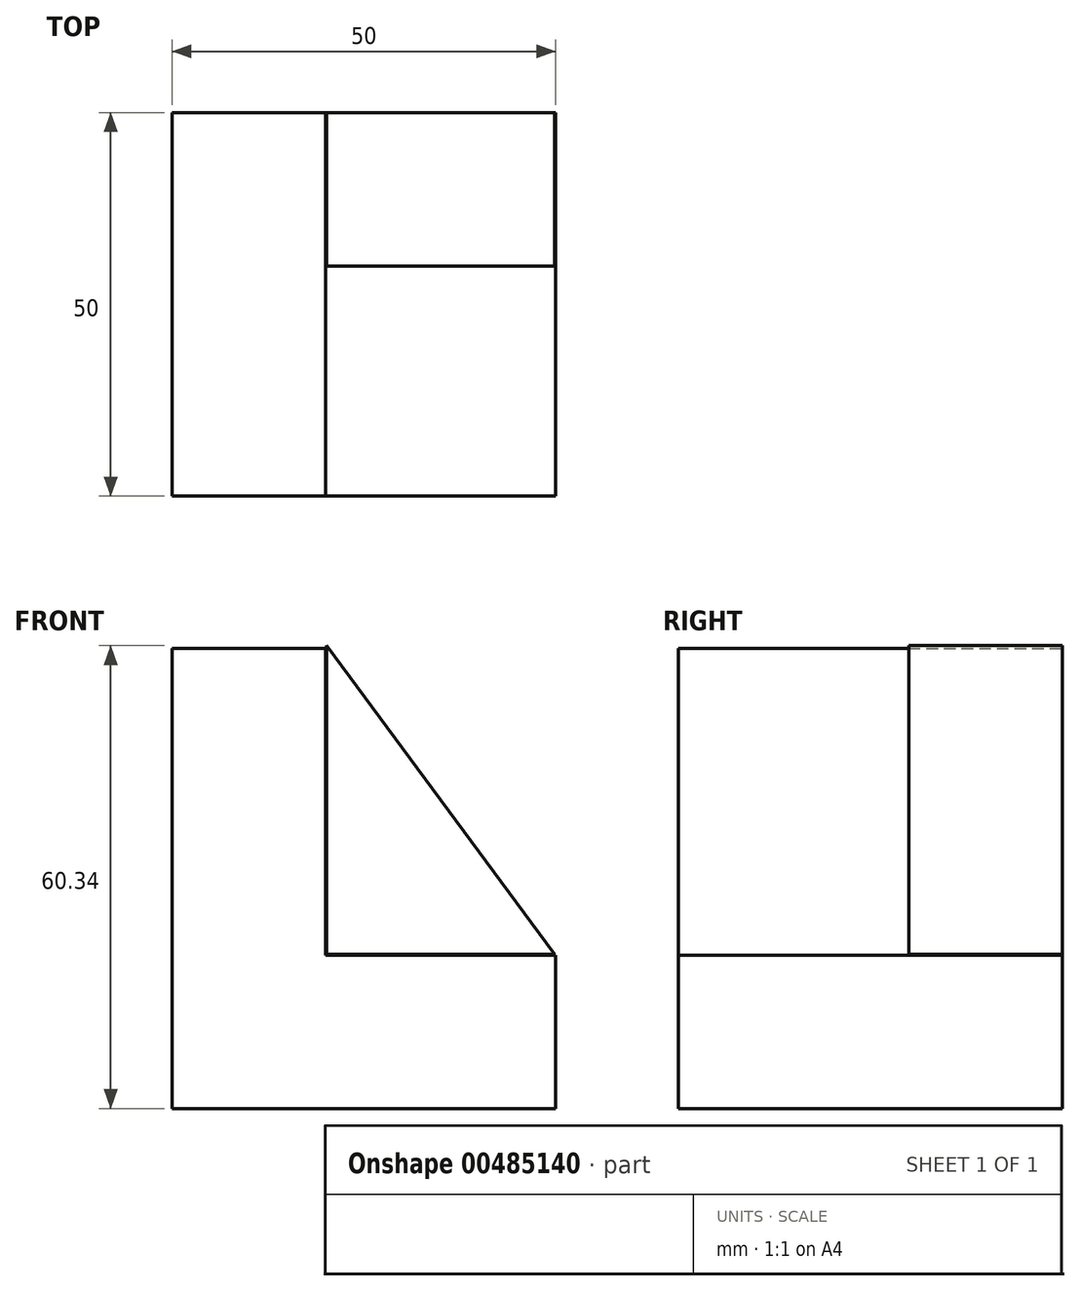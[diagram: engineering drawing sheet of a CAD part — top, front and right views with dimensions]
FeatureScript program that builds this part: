
annotation { "Feature Type Name" : "Feature", "Feature Type Description" : "" }
export const myFeature = defineFeature(function(context is Context, id is Id, definition is map)
    precondition{}
    {
        {
            var Q0;
            Q0=qCreatedBy(makeId("Front.planeOp"),FACE);
            var sketch = newSketch(context, id + "F0", { "sketchPlane" : qUnion([Q0])});
            skLineSegment(sketch, "E0", {"start": v(0, 0) * mm, "end": v(0, 60) * mm});
            skLineSegment(sketch, "E1", {"start": v(0, 60) * mm, "end": v(20, 60) * mm});
            skLineSegment(sketch, "E2", {"start": v(20, 60) * mm, "end": v(20, 20) * mm});
            skLineSegment(sketch, "E3", {"start": v(20, 20) * mm, "end": v(50, 20) * mm});
            skLineSegment(sketch, "E4", {"start": v(50, 20) * mm, "end": v(50, 0) * mm});
            skLineSegment(sketch, "E5", {"start": v(50, 0) * mm, "end": v(0, 0) * mm});
            skSolve(sketch);
        }
        {
            var Q0;
            Q0 = qSketchRegion(id + "F0", true);
            extrude(context, id + "F1", {"entities" : qUnion([Q0]), "depth" : 50 * mm});
        }
        {
            var Q0;
            Q0=qCreatedBy(makeId("Front.planeOp"),FACE);
            var sketch = newSketch(context, id + "F2", { "sketchPlane" : qUnion([Q0])});
            skLineSegment(sketch, "E6", {"start": v(20.11, 60.34) * mm, "end": v(20.11, 20.11) * mm});
            skLineSegment(sketch, "E7", {"start": v(20.11, 20.11) * mm, "end": v(49.86, 20.11) * mm});
            skLineSegment(sketch, "E8", {"start": v(49.86, 20.11) * mm, "end": v(20.11, 60.34) * mm});
            skSolve(sketch);
        }
        {
            var Q0;
            Q0 = qSketchRegion(id + "F2", true);
            extrude(context, id + "F3", {"entities" : qUnion([Q0]), "depth" : 20 * mm});
        }
    });
